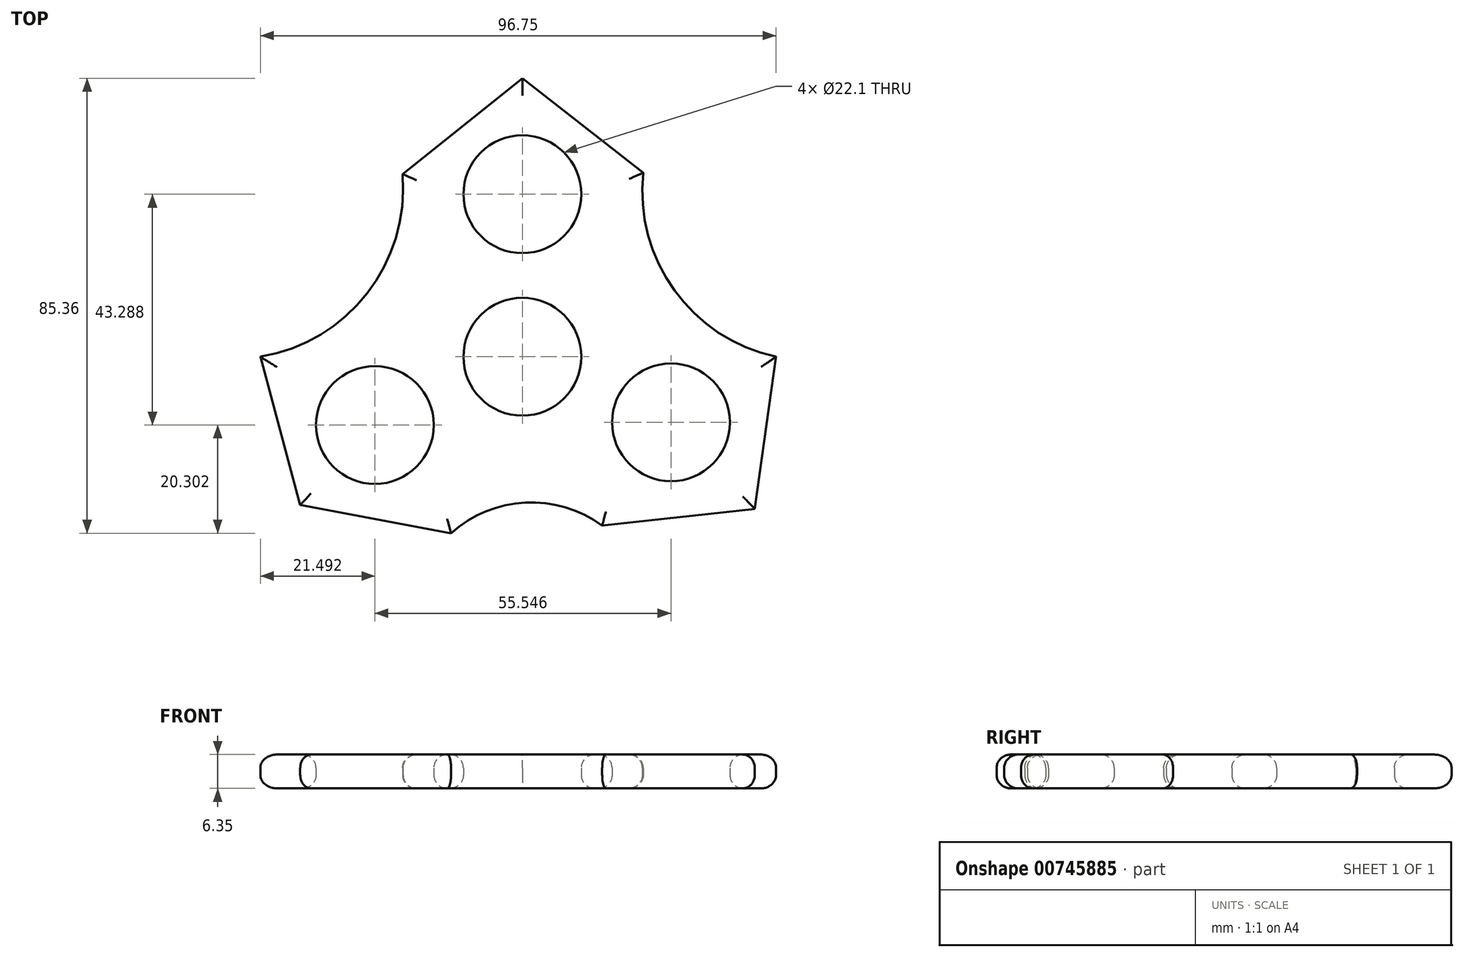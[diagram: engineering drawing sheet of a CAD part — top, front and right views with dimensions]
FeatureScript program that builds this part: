
annotation { "Feature Type Name" : "Feature", "Feature Type Description" : "" }
export const myFeature = defineFeature(function(context is Context, id is Id, definition is map)
    precondition{}
    {
        {
            var Q0;
            Q0=qCreatedBy(makeId("Top.planeOp"),FACE);
            var sketch = newSketch(context, id + "F0", { "sketchPlane" : qUnion([Q0])});
            skCircle(sketch, "E0", {"center": v(0, 0) * mm, "radius": 11.05 * mm});
            skCircle(sketch, "E1", {"center": v(0, 0) * mm, "radius": 13.97 * mm});
            skLineSegment(sketch, "E2", {"start": v(0, 0) * mm, "end": v(0, 30.48) * mm});
            skLineSegment(sketch, "E3", {"start": v(0, 0) * mm, "end": v(-27.66, -12.8) * mm});
            skLineSegment(sketch, "E4", {"start": v(0, 0) * mm, "end": v(27.89, -12.3) * mm});
            skCircle(sketch, "E5", {"center": v(27.89, -12.3) * mm, "radius": 11.05 * mm});
            skCircle(sketch, "E6", {"center": v(27.89, -12.3) * mm, "radius": 15.24 * mm});
            skCircle(sketch, "E7", {"center": v(0, 30.48) * mm, "radius": 11.05 * mm});
            skCircle(sketch, "E8", {"center": v(0, 30.48) * mm, "radius": 15.24 * mm});
            skCircle(sketch, "E9", {"center": v(-27.66, -12.8) * mm, "radius": 11.05 * mm});
            skCircle(sketch, "E10", {"center": v(-27.66, -12.8) * mm, "radius": 15.24 * mm});
            skLineSegment(sketch, "E11", {"start": v(0, 52.25) * mm, "end": v(-22.48, 34.27) * mm});
            skLineSegment(sketch, "E12", {"start": v(0, 52.25) * mm, "end": v(22.7, 34.51) * mm});
            skLineSegment(sketch, "E13", {"start": v(43.6, -28.52) * mm, "end": v(47.6, 0) * mm});
            skLineSegment(sketch, "E14", {"start": v(43.6, -28.52) * mm, "end": v(14.98, -31.7) * mm});
            skLineSegment(sketch, "E15", {"start": v(-41.67, -27.81) * mm, "end": v(-49.15, 0) * mm});
            skLineSegment(sketch, "E16", {"start": v(-41.67, -27.81) * mm, "end": v(-13.36, -33.11) * mm});
            skArc(sketch, "E17", {"start": v(-49.15, 0) * mm, "mid": v(-29.1, 11.9) * mm, "end": v(-22.48, 34.27) * mm});
            skArc(sketch, "E18", {"start": v(22.7, 34.51) * mm, "mid": v(28.52, 12.47) * mm, "end": v(47.6, 0) * mm});
            skArc(sketch, "E19", {"start": v(14.98, -31.7) * mm, "mid": v(0.56, -27.34) * mm, "end": v(-13.36, -33.11) * mm});
            skSolve(sketch);
        }
        {
            var Q0;
            Q0=makeQuery(id+"F0.imprint","IMPRINT",FACE,{"disambiguationData":[TD([[makeQuery(id+"F0.imprint","IMPRINT",EDGE,{"derivedFrom":sQuery(id+"F0.wireOp",EDGE,"E6")}),-1.0]])]});
            var Q1;
            Q1=makeQuery(id+"F0.imprint","IMPRINT",FACE,{"disambiguationData":[TD([[makeQuery(id+"F0.imprint","IMPRINT",EDGE,{"derivedFrom":sQuery(id+"F0.wireOp",EDGE,"E7")}),-1.0]])]});
            var Q2;
            {var subQ0=sQuery(id+"F0.wireOp",EDGE,"E2");var subQ1=sQuery(id+"F0.wireOp",EDGE,"E0");var subQ2=makeQuery(id+"F0.imprint","INTERSECT",VERTEX,{"derivedFrom":[subQ1,subQ0]});Q2=makeQuery(id+"F0.imprint","IMPRINT",FACE,{"disambiguationData":[TD([[makeQuery(id+"F0.imprint","IMPRINT",EDGE,{"disambiguationData":[TD([[subQ2,1.0]])],"derivedFrom":subQ1}),-1.0]])]});}
            var Q3;
            {var subQ0=sQuery(id+"F0.wireOp",EDGE,"E3");var subQ1=sQuery(id+"F0.wireOp",EDGE,"E0");var subQ2=makeQuery(id+"F0.imprint","INTERSECT",VERTEX,{"derivedFrom":[subQ1,subQ0]});Q3=makeQuery(id+"F0.imprint","IMPRINT",FACE,{"disambiguationData":[TD([[makeQuery(id+"F0.imprint","IMPRINT",EDGE,{"disambiguationData":[TD([[subQ2,1.0]])],"derivedFrom":subQ1}),-1.0]])]});}
            var Q4;
            {var subQ0=sQuery(id+"F0.wireOp",EDGE,"E3");var subQ1=sQuery(id+"F0.wireOp",EDGE,"E0");var subQ2=makeQuery(id+"F0.imprint","INTERSECT",VERTEX,{"derivedFrom":[subQ1,subQ0]});Q4=makeQuery(id+"F0.imprint","IMPRINT",FACE,{"disambiguationData":[TD([[makeQuery(id+"F0.imprint","IMPRINT",EDGE,{"disambiguationData":[TD([[subQ2,-1.0]])],"derivedFrom":subQ1}),-1.0]])]});}
            var Q5;
            Q5=makeQuery(id+"F0.imprint","IMPRINT",FACE,{"disambiguationData":[TD([[makeQuery(id+"F0.imprint","IMPRINT",EDGE,{"derivedFrom":sQuery(id+"F0.wireOp",EDGE,"E9")}),-1.0]])]});
            var Q6;
            Q6=makeQuery(id+"F0.imprint","IMPRINT",FACE,{"disambiguationData":[TD([[makeQuery(id+"F0.imprint","IMPRINT",EDGE,{"derivedFrom":sQuery(id+"F0.wireOp",EDGE,"E5")}),-1.0]])]});
            extrude(context, id + "F1", {"entities" : qUnion([Q0, Q1, Q2, Q3, Q4, Q5, Q6]), "depth" : 6.35 * mm, "offsetDistance" : 25.4 * mm});
        }
        {
            var Q0;
            Q0=makeQuery(id+"F1.opExtrude","CAP_EDGE",EDGE,{"disambiguationData":[OSD([sQuery(id+"F0.wireOp",EDGE,"E7")])],"isStart":false});
            var Q1;
            Q1=makeQuery(id+"F1.opExtrude","CAP_EDGE",EDGE,{"disambiguationData":[OSD([sQuery(id+"F0.wireOp",EDGE,"E5")])],"isStart":false});
            var Q2;
            Q2=makeQuery(id+"F1.opExtrude","CAP_EDGE",EDGE,{"disambiguationData":[OSD([sQuery(id+"F0.wireOp",EDGE,"E9")])],"isStart":false});
            var Q3;
            Q3=makeQuery(id+"F1.opExtrude","CAP_EDGE",EDGE,{"disambiguationData":[OSD([sQuery(id+"F0.wireOp",EDGE,"E19")])],"isStart":false});
            var Q4;
            Q4=makeQuery(id+"F1.opExtrude","CAP_EDGE",EDGE,{"disambiguationData":[OSD([sQuery(id+"F0.wireOp",EDGE,"E14")])],"isStart":false});
            var Q5;
            Q5=makeQuery(id+"F1.opExtrude","CAP_EDGE",EDGE,{"disambiguationData":[OSD([sQuery(id+"F0.wireOp",EDGE,"E13")])],"isStart":false});
            var Q6;
            Q6=makeQuery(id+"F1.opExtrude","CAP_EDGE",EDGE,{"disambiguationData":[OSD([sQuery(id+"F0.wireOp",EDGE,"E18")])],"isStart":false});
            var Q7;
            Q7=makeQuery(id+"F1.opExtrude","CAP_EDGE",EDGE,{"disambiguationData":[OSD([sQuery(id+"F0.wireOp",EDGE,"E12")])],"isStart":false});
            var Q8;
            Q8=makeQuery(id+"F1.opExtrude","CAP_EDGE",EDGE,{"disambiguationData":[OSD([sQuery(id+"F0.wireOp",EDGE,"E11")])],"isStart":false});
            var Q9;
            Q9=makeQuery(id+"F1.opExtrude","CAP_EDGE",EDGE,{"disambiguationData":[OSD([sQuery(id+"F0.wireOp",EDGE,"E17")])],"isStart":false});
            var Q10;
            Q10=makeQuery(id+"F1.opExtrude","CAP_EDGE",EDGE,{"disambiguationData":[OSD([sQuery(id+"F0.wireOp",EDGE,"E15")])],"isStart":false});
            var Q11;
            Q11=makeQuery(id+"F1.opExtrude","CAP_EDGE",EDGE,{"disambiguationData":[OSD([sQuery(id+"F0.wireOp",EDGE,"E16")])],"isStart":false});
            var Q12;
            Q12=makeQuery(id+"F1.opExtrude","CAP_EDGE",EDGE,{"disambiguationData":[OSD([sQuery(id+"F0.wireOp",EDGE,"E0")])],"isStart":false});
            fillet(context, id + "F2", {"entities" : qUnion([Q0, Q1, Q2, Q3, Q4, Q5, Q6, Q7, Q8, Q9, Q10, Q11, Q12]), "radius" : 2.54 * mm, "tangentPropagation" : true, "allowEdgeOverflow" : false});
        }
        {
            var Q0;
            Q0=makeQuery(id+"F1.opExtrude","CAP_EDGE",EDGE,{"disambiguationData":[OSD([sQuery(id+"F0.wireOp",EDGE,"E0")])],"isStart":true});
            var Q1;
            Q1=makeQuery(id+"F1.opExtrude","CAP_EDGE",EDGE,{"disambiguationData":[OSD([sQuery(id+"F0.wireOp",EDGE,"E9")])],"isStart":true});
            var Q2;
            Q2=makeQuery(id+"F1.opExtrude","CAP_EDGE",EDGE,{"disambiguationData":[OSD([sQuery(id+"F0.wireOp",EDGE,"E5")])],"isStart":true});
            var Q3;
            Q3=makeQuery(id+"F1.opExtrude","CAP_EDGE",EDGE,{"disambiguationData":[OSD([sQuery(id+"F0.wireOp",EDGE,"E7")])],"isStart":true});
            var Q4;
            Q4=makeQuery(id+"F1.opExtrude","CAP_EDGE",EDGE,{"disambiguationData":[OSD([sQuery(id+"F0.wireOp",EDGE,"E18")])],"isStart":true});
            var Q5;
            Q5=makeQuery(id+"F1.opExtrude","CAP_EDGE",EDGE,{"disambiguationData":[OSD([sQuery(id+"F0.wireOp",EDGE,"E13")])],"isStart":true});
            var Q6;
            Q6=makeQuery(id+"F1.opExtrude","CAP_EDGE",EDGE,{"disambiguationData":[OSD([sQuery(id+"F0.wireOp",EDGE,"E14")])],"isStart":true});
            var Q7;
            Q7=makeQuery(id+"F1.opExtrude","CAP_EDGE",EDGE,{"disambiguationData":[OSD([sQuery(id+"F0.wireOp",EDGE,"E19")])],"isStart":true});
            var Q8;
            Q8=makeQuery(id+"F1.opExtrude","CAP_EDGE",EDGE,{"disambiguationData":[OSD([sQuery(id+"F0.wireOp",EDGE,"E16")])],"isStart":true});
            var Q9;
            Q9=makeQuery(id+"F1.opExtrude","CAP_EDGE",EDGE,{"disambiguationData":[OSD([sQuery(id+"F0.wireOp",EDGE,"E15")])],"isStart":true});
            var Q10;
            Q10=makeQuery(id+"F1.opExtrude","CAP_EDGE",EDGE,{"disambiguationData":[OSD([sQuery(id+"F0.wireOp",EDGE,"E17")])],"isStart":true});
            var Q11;
            Q11=makeQuery(id+"F1.opExtrude","CAP_EDGE",EDGE,{"disambiguationData":[OSD([sQuery(id+"F0.wireOp",EDGE,"E11")])],"isStart":true});
            var Q12;
            Q12=makeQuery(id+"F1.opExtrude","CAP_EDGE",EDGE,{"disambiguationData":[OSD([sQuery(id+"F0.wireOp",EDGE,"E12")])],"isStart":true});
            fillet(context, id + "F3", {"entities" : qUnion([Q0, Q1, Q2, Q3, Q4, Q5, Q6, Q7, Q8, Q9, Q10, Q11, Q12]), "radius" : 2.54 * mm, "tangentPropagation" : true, "allowEdgeOverflow" : false});
        }
    });
